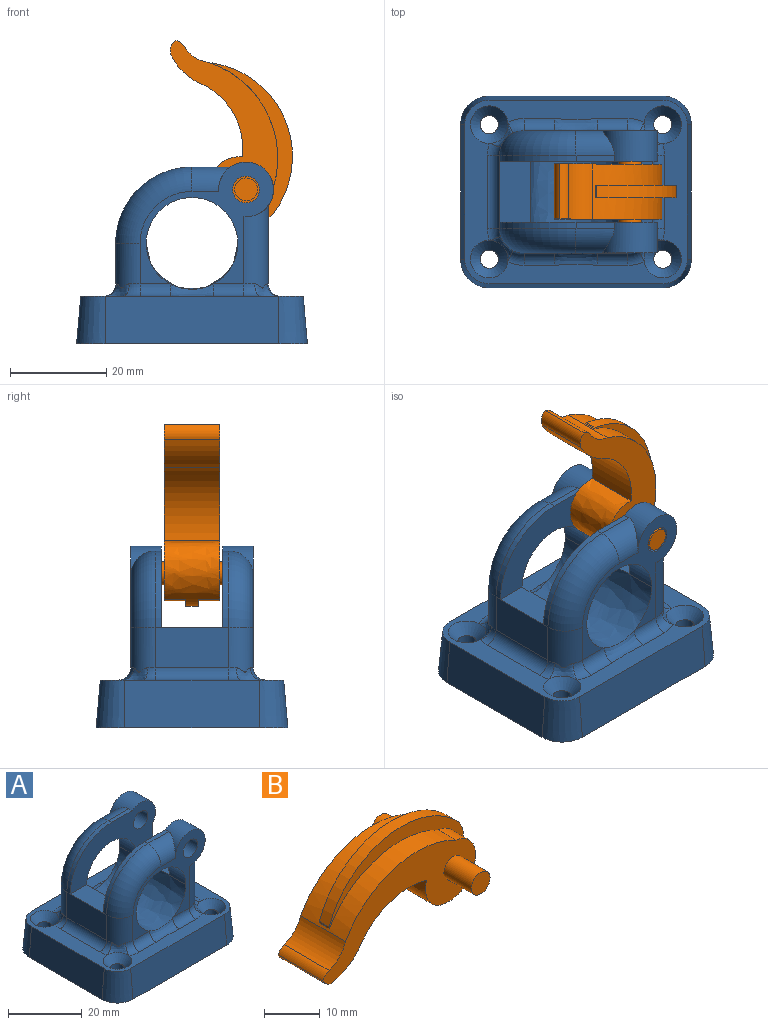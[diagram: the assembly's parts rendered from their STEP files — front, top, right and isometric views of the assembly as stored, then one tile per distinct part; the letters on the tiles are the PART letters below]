
ASSEMBLY  parts=2 mates=1
PART A: 65 faces, bbox 47.9x39.8x38 mm
  f0: plane 16.35x15.24mm, normal (1,0,0), area 148.4mm2, adj f6,f7,f9,f14,f24,f25,f26,f53
  f1: plane 15.24x8.41mm, normal (-1,0,0), area 128.2mm2, adj f4,f5,f10,f16,f23,f56
  f2: plane 27.72x25.7mm, normal (0,-1,0), area 168.2mm2, adj f5,f7,f13,f14,f17,f18,f21,f22
  f3: plane 27.72x25.7mm, normal (0,1,0), area 168.2mm2, adj f4,f6,f9,f11,f12,f13,f19,f20
  f4: cylinder r=5.08mm len=9.27mm, axis (0,0,-1), area 68.7mm2, adj f1,f3,f19,f58,f60,f62
  f5: cylinder r=5.08mm len=9.27mm, axis (0,0,1), area 68.7mm2, adj f1,f2,f21,f50,f52,f54
  f6: cylinder r=5.08mm len=17.2mm, axis (0,0,1), area 122.5mm2, adj f0,f3,f9,f55,f57,f59
  f7: cylinder r=5.08mm len=17.2mm, axis (0,0,-1), area 122.5mm2, adj f0,f2,f14,f47,f49,f51
  f8: plane 7.94x1.27mm, normal (0,0,1), area 10.1mm2, adj f9,f10,f20,f24
  f9: cylinder r=5.69mm len=11.39mm, axis (0,1,0), area 116.2mm2, adj f0,f3,f6,f8,f20,f24
  f10: cylinder r=15.88mm len=15.88mm, axis (0,1,0), area 31.7mm2, adj f1,f8,f19,f24
  f11: cylinder r=9.53mm len=19.05mm, axis (0,1,0), area 190mm2, adj f3,f13,f24
  f12: cylinder r=2.78mm len=6.35mm, axis (0,1,0), area 110.9mm2, adj f3,f24
  f13: extruded ~25.4x19.05mm, area 760.1mm2, adj f2,f3,f11,f17,f23,f26,f46,f63
  f14: cylinder r=5.69mm len=11.39mm, axis (0,1,0), area 116.2mm2, adj f0,f2,f7,f15,f22,f25
  f15: plane 7.94x1.27mm, normal (0,0,1), area 10.1mm2, adj f14,f16,f22,f25
  f16: cylinder r=15.88mm len=15.88mm, axis (0,1,0), area 31.7mm2, adj f1,f15,f21,f25
  f17: cylinder r=9.53mm len=19.05mm, axis (0,1,0), area 190mm2, adj f2,f13,f25
  f18: cylinder r=2.78mm len=6.35mm, axis (0,1,0), area 110.9mm2, adj f2,f25
  f19: torus R=10.79mm, axis (0,-1,0), area 175.8mm2, adj f3,f4,f10,f20
  f20: cylinder r=5.08mm len=7.94mm, axis (-1,0,0), area 53.8mm2, adj f3,f8,f9,f19
  f21: torus R=10.79mm, axis (0,-1,0), area 175.8mm2, adj f2,f5,f16,f22
  f22: cylinder r=5.08mm len=7.94mm, axis (1,0,0), area 53.8mm2, adj f2,f14,f15,f21
  f23: plane 12.7x6.35mm, normal (0,0,1), area 80.6mm2, adj f1,f13,f24,f25
  f24: plane 32.8x16.92mm, normal (0,-1,0), area 291.7mm2, adj f0,f8,f9,f10,f11,f12,f23,f26
  f25: plane 32.8x16.92mm, normal (0,1,0), area 291.7mm2, adj f0,f14,f15,f16,f17,f18,f23,f26
  f26: plane 12.7x6.35mm, normal (0,0,1), area 80.6mm2, adj f0,f13,f24,f25
  f27: plane 27.94x9.84mm, normal (1,0,0.09), area 276.1mm2, adj f28,f30,f34,f36
  f28: plane 46.2x38.1mm, normal (0,0,1), area 507.3mm2, adj f27,f29,f31,f32,f33,f34,f35,f36
  f29: plane 27.94x9.84mm, normal (-1,0,0.09), area 276.1mm2, adj f28,f30,f33,f35
  f30: plane 47.93x39.82mm, normal (0,0,-1), area 1833mm2, adj f27,f29,f31,f32,f33,f34,f35,f36
  f31: plane 36.04x9.84mm, normal (0,-1,0.09), area 356.2mm2, adj f28,f30,f35,f36
  f32: plane 36.04x9.84mm, normal (0,1,0.09), area 356.2mm2, adj f28,f30,f33,f34
  f33: cone r=5.08mm half-angle=5deg, axis (0,0,-1), area 85.5mm2, adj f28,f29,f30,f32
  f34: cone r=5.08mm half-angle=5deg, axis (0,0,-1), area 85.5mm2, adj f27,f28,f30,f32
  f35: cone r=5.08mm half-angle=5deg, axis (0,0,-1), area 85.5mm2, adj f28,f29,f30,f31
  f36: cone r=5.08mm half-angle=5deg, axis (0,0,-1), area 85.5mm2, adj f27,f28,f30,f31
  f37: cylinder r=1.9mm len=7.54mm, axis (0,0,1), area 90mm2, adj f30,f38
  f38: cone r=1.9mm half-angle=41deg, axis (0,0,1), area 55.5mm2, adj f28,f37,f60
  f39: cylinder r=1.9mm len=7.54mm, axis (0,0,1), area 90mm2, adj f30,f40
  f40: cone r=1.9mm half-angle=41deg, axis (0,0,1), area 55.5mm2, adj f28,f39,f57
  f41: cylinder r=1.9mm len=7.54mm, axis (0,0,1), area 90mm2, adj f30,f42
  f42: cone r=1.9mm half-angle=41deg, axis (0,0,1), area 55.5mm2, adj f28,f41,f49
  f43: cylinder r=1.9mm len=7.54mm, axis (0,0,1), area 90mm2, adj f30,f44
  f44: cone r=1.9mm half-angle=41deg, axis (0,0,1), area 55.5mm2, adj f28,f43,f52
  f45: cylinder r=2.54mm len=6.33mm, axis (1,0,0), area 25.3mm2, adj f2,f28,f46,f47
  f46: bspline ~9.55x2.72mm, area 28.8mm2, adj f13,f28,f45,f48
  f47: torus R=7.62mm, axis (0,0,-1), area 10.9mm2, adj f7,f28,f45,f49
  f48: cylinder r=2.54mm len=6.33mm, axis (1,0,0), area 25.3mm2, adj f2,f28,f46,f50
  f49: bspline ~5.21x4.98mm, area 11.4mm2, adj f7,f42,f47,f51
  f50: torus R=7.62mm, axis (0,0,-1), area 10.9mm2, adj f5,f28,f48,f52
  f51: torus R=7.62mm, axis (0,0,-1), area 7.8mm2, adj f7,f28,f49,f53
  f52: bspline ~5.21x4.98mm, area 11.4mm2, adj f5,f44,f50,f54
  f53: cylinder r=2.54mm len=15.24mm, axis (0,1,0), area 60.8mm2, adj f0,f28,f51,f55
  f54: torus R=7.62mm, axis (0,0,-1), area 7.8mm2, adj f5,f28,f52,f56
  f55: torus R=7.62mm, axis (0,0,-1), area 7.8mm2, adj f6,f28,f53,f57
  f56: cylinder r=2.54mm len=15.24mm, axis (0,-1,0), area 60.8mm2, adj f1,f28,f54,f58
  f57: bspline ~5.21x4.98mm, area 11.4mm2, adj f6,f40,f55,f59
  f58: torus R=7.62mm, axis (0,0,-1), area 7.8mm2, adj f4,f28,f56,f60
  f59: torus R=7.62mm, axis (0,0,-1), area 10.9mm2, adj f6,f28,f57,f61
  f60: bspline ~5.21x4.98mm, area 11.4mm2, adj f4,f38,f58,f62
  f61: cylinder r=2.54mm len=6.33mm, axis (-1,0,0), area 25.3mm2, adj f3,f28,f59,f63
  f62: torus R=7.62mm, axis (0,0,-1), area 10.9mm2, adj f4,f28,f60,f64
  f63: bspline ~9.55x2.72mm, area 28.8mm2, adj f13,f28,f61,f64
  f64: cylinder r=2.54mm len=6.33mm, axis (-1,0,0), area 25.3mm2, adj f3,f28,f62,f63
PART B: 21 faces, bbox 40.2x25.4x21.2 mm
  f0: plane 4.45x1.04mm, normal (1,0,0), area 4.6mm2, adj f1,f3,f9,f18
  f1: cylinder r=5.69mm len=8.94mm, axis (0,-1,0), area 52.3mm2, adj f0,f2,f9,f18
  f2: cylinder r=20.94mm len=28.08mm, axis (0,-1,0), area 289.9mm2, adj f1,f5,f6,f9,f10,f16,f17,f18
  f3: extruded ~14.03x11.65mm, area 225.9mm2, adj f0,f4,f8,f9,f10,f15,f17,f18
  f4: plane 4.45x1.04mm, normal (1,0,0), area 4.6mm2, adj f3,f5,f10,f17
  f5: cylinder r=5.69mm len=8.94mm, axis (0,-1,0), area 52.3mm2, adj f2,f4,f10,f17
  f6: cylinder r=6.58mm len=11.43mm, axis (0,-1,0), area 70.8mm2, adj f2,f9,f10,f20
  f7: cylinder r=11.57mm len=11.43mm, axis (0,-1,0), area 95.4mm2, adj f8,f9,f10,f19
  f8: cylinder r=14.83mm len=16.69mm, axis (0,-1,0), area 216.3mm2, adj f3,f7,f9,f10
  f9: plane 38.84x18.12mm, normal (0,1,0), area 291.8mm2, adj f0,f1,f2,f3,f6,f7,f8,f13
  f10: plane 38.84x18.12mm, normal (0,-1,0), area 291.8mm2, adj f2,f3,f4,f5,f6,f7,f8,f12
  f11: plane 4.76x4.76mm, normal (0,-1,0), area 17.8mm2, adj f12
  f12: cylinder r=2.38mm len=6.99mm, axis (0,1,0), area 104.5mm2, adj f10,f11
  f13: cylinder r=2.38mm len=6.99mm, axis (0,1,0), area 104.5mm2, adj f9,f14
  f14: plane 4.76x4.76mm, normal (0,1,0), area 17.8mm2, adj f13
  f15: cylinder r=19.71mm len=33.11mm, axis (0,1,0), area 102.8mm2, adj f3,f16,f17,f18
  f16: plane 2.54x0.36mm, normal (-1,0,0), area 0.9mm2, adj f2,f15,f17,f18
  f17: plane 34.12x15.44mm, normal (0,-1,0), area 96.7mm2, adj f2,f3,f4,f5,f15,f16
  f18: plane 34.12x15.44mm, normal (0,1,0), area 96.7mm2, adj f0,f1,f2,f3,f15,f16
  f19: cylinder r=2.54mm len=11.43mm, axis (0,-1,0), area 41.6mm2, adj f7,f9,f10,f20
  f20: cylinder r=2.54mm len=11.43mm, axis (0,-1,0), area 25.7mm2, adj f6,f9,f10,f19
PLACE A at identity fixed
PLACE B rot(axis=(0,1,0),79.1deg) t=(-1.92,0,20.13)mm
MATE revolute B.f1 <-> A.f9  axis (0,-1,0) through (11.23,-12.7,11.23)mm
